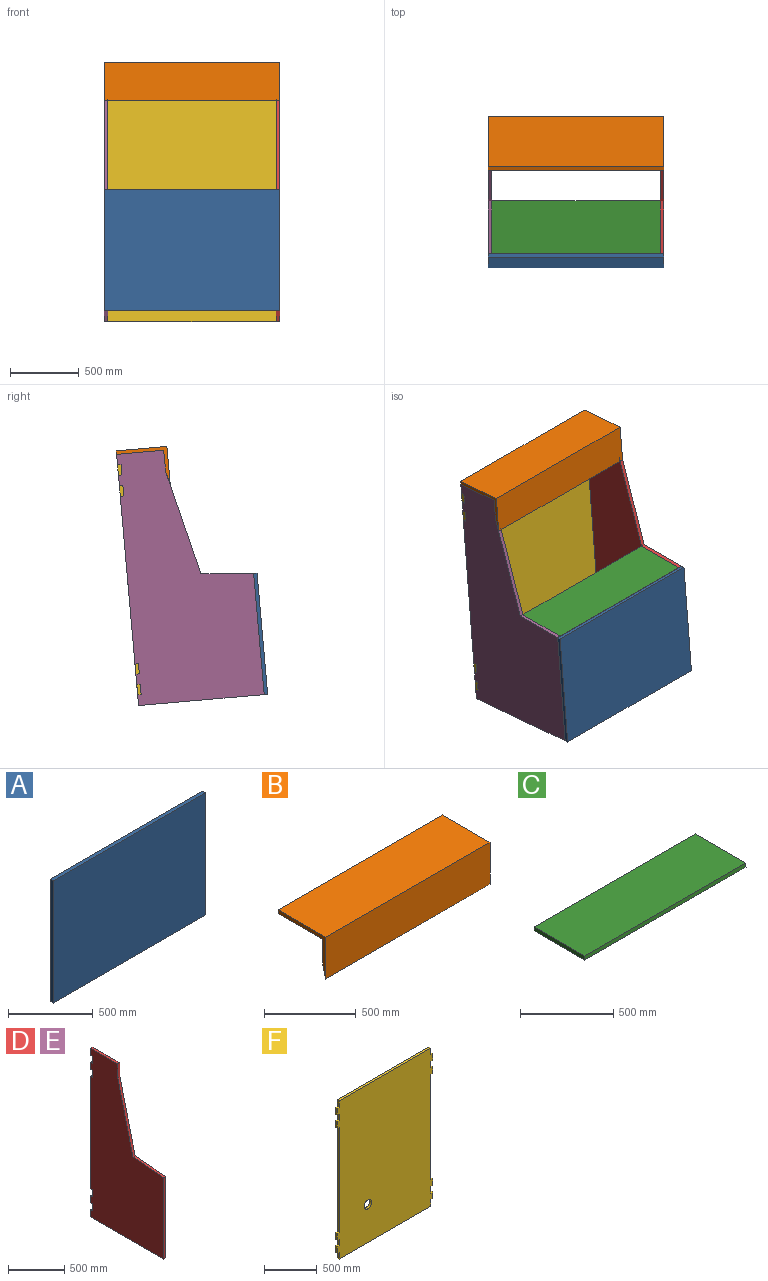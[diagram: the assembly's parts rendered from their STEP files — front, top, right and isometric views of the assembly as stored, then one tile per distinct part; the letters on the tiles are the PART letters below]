
ASSEMBLY  parts=6 mates=12
PART A: 6 faces, bbox 1270x25.4x881.1 mm
  f0: plane 881.07x25.4mm, normal (1,0,0), area 22379.1mm2, adj f1,f3,f4,f5
  f1: plane 1270x25.4mm, normal (0,0,1), area 32258mm2, adj f0,f2,f4,f5
  f2: plane 881.07x25.4mm, normal (-1,0,0), area 22379.1mm2, adj f1,f3,f4,f5
  f3: plane 1270x25.4mm, normal (0,0,-1), area 32258mm2, adj f0,f2,f4,f5
  f4: plane 1270x881.07mm, normal (0,-1,0), area 1118954.9mm2, adj f0,f1,f2,f3
  f5: plane 1270x881.07mm, normal (0,1,0), area 1118954.9mm2, adj f0,f1,f2,f3
PART B: 8 faces, bbox 1270x368.3x279.4 mm
  f0: plane 1270x342.9mm, normal (0,0,-1), area 435483mm2, adj f1,f2,f3,f6
  f1: plane 368.3x279.4mm, normal (1,0,0), area 14516.1mm2, adj f0,f2,f4,f5,f6,f7
  f2: plane 1270x25.4mm, normal (0,1,0), area 32258mm2, adj f0,f1,f3,f5
  f3: plane 368.3x279.4mm, normal (-1,0,0), area 14516.1mm2, adj f0,f2,f4,f5,f6,f7
  f4: plane 1270x279.4mm, normal (0,-1,0), area 354838mm2, adj f1,f3,f5,f7
  f5: plane 1270x368.3mm, normal (0,0,1), area 467741mm2, adj f1,f2,f3,f4
  f6: plane 1270x152.4mm, normal (0,1,0), area 193548mm2, adj f0,f1,f3,f7
  f7: plane 1270x101.6mm, normal (0,0.97,-0.24), area 133003.1mm2, adj f1,f3,f4,f6
PART C: 6 faces, bbox 1219.2x384.7x25.4 mm
  f0: plane 384.68x25.4mm, normal (1,0,0), area 9742.6mm2, adj f1,f3,f4,f5
  f1: plane 1219.2x25.4mm, normal (0,1,0), area 30967.7mm2, adj f0,f2,f3,f4
  f2: plane 384.68x25.4mm, normal (-1,0,0), area 9742.6mm2, adj f1,f3,f4,f5
  f3: plane 1219.2x382.46mm, normal (0,0,1), area 466289.6mm2, adj f0,f1,f2,f5
  f4: plane 1219.2x384.68mm, normal (0,0,-1), area 468998.9mm2, adj f0,f1,f2,f5
  f5: plane 1219.2x25.4mm, normal (0,-1,0.09), area 31086mm2, adj f0,f2,f3,f4
PART D: 25 faces, bbox 25.4x914.4x1828.8 mm
  f0: plane 76.2x25.4mm, normal (0,1,0), area 1935.5mm2, adj f4,f5,f20,f24
  f1: plane 1219.2x25.4mm, normal (0,1,0), area 30967.7mm2, adj f4,f5,f16,f19
  f2: plane 76.2x25.4mm, normal (0,1,0), area 1935.5mm2, adj f4,f5,f14,f18
  f3: plane 76.2x25.4mm, normal (0,1,0), area 1935.5mm2, adj f4,f5,f9,f13
  f4: plane 1828.8x914.4mm, normal (1,0,0), area 1208163.7mm2, adj f0,f1,f2,f3,f6,f7,f8,f9
  f5: plane 1828.8x914.4mm, normal (-1,0,0), area 1208163.7mm2, adj f0,f1,f2,f3,f6,f7,f8,f9
  f6: plane 762x190.5mm, normal (0,-0.97,0.24), area 19950.5mm2, adj f4,f5,f7,f12
  f7: plane 381x33.33mm, normal (0,-0.09,1), area 9714.4mm2, adj f4,f5,f6,f8
  f8: plane 881.07x25.4mm, normal (0,-1,0), area 22379.1mm2, adj f4,f5,f7,f9
  f9: plane 914.4x25.4mm, normal (0,0,-1), area 23225.8mm2, adj f3,f4,f5,f8
  f10: plane 76.2x25.4mm, normal (0,1,0), area 1935.5mm2, adj f4,f5,f11,f22
  f11: plane 342.9x25.4mm, normal (0,0,1), area 8709.7mm2, adj f4,f5,f10,f12
  f12: plane 152.4x25.4mm, normal (0,-1,0), area 3871mm2, adj f4,f5,f6,f11
  f13: plane 25.4x25.4mm, normal (0,0,1), area 645.2mm2, adj f3,f4,f5,f15
  f14: plane 25.4x25.4mm, normal (0,0,-1), area 645.2mm2, adj f2,f4,f5,f15
  f15: plane 76.2x25.4mm, normal (0,1,0), area 1935.5mm2, adj f4,f5,f13,f14
  f16: plane 25.4x25.4mm, normal (0,0,-1), area 645.2mm2, adj f1,f4,f5,f17
  f17: plane 76.2x25.4mm, normal (0,1,0), area 1935.5mm2, adj f4,f5,f16,f18
  f18: plane 25.4x25.4mm, normal (0,0,1), area 645.2mm2, adj f2,f4,f5,f17
  f19: plane 25.4x25.4mm, normal (0,0,1), area 645.2mm2, adj f1,f4,f5,f21
  f20: plane 25.4x25.4mm, normal (0,0,-1), area 645.2mm2, adj f0,f4,f5,f21
  f21: plane 76.2x25.4mm, normal (0,1,0), area 1935.5mm2, adj f4,f5,f19,f20
  f22: plane 25.4x25.4mm, normal (0,0,-1), area 645.2mm2, adj f4,f5,f10,f23
  f23: plane 76.2x25.4mm, normal (0,1,0), area 1935.5mm2, adj f4,f5,f22,f24
  f24: plane 25.4x25.4mm, normal (0,0,1), area 645.2mm2, adj f0,f4,f5,f23
PART E: same geometry as D
PART F: 39 faces, bbox 1270x25.4x1828.8 mm
  f0: plane 1219.2x25.4mm, normal (1,0,0), area 30967.7mm2, adj f12,f13,f30,f35
  f1: plane 76.2x25.4mm, normal (1,0,0), area 1935.5mm2, adj f12,f13,f33,f36
  f2: plane 76.2x25.4mm, normal (1,0,0), area 1935.5mm2, adj f12,f13,f26,f29
  f3: plane 76.2x25.4mm, normal (1,0,0), area 1935.5mm2, adj f9,f12,f13,f27
  f4: plane 76.2x25.4mm, normal (-1,0,0), area 1935.5mm2, adj f12,f13,f21,f24
  f5: plane 76.2x25.4mm, normal (-1,0,0), area 1935.5mm2, adj f11,f12,f13,f20
  f6: plane 1219.2x25.4mm, normal (-1,0,0), area 30967.7mm2, adj f12,f13,f18,f23
  f7: plane 76.2x25.4mm, normal (-1,0,0), area 1935.5mm2, adj f12,f13,f14,f17
  f8: plane 76.2x25.4mm, normal (1,0,0), area 1935.5mm2, adj f11,f12,f13,f32
  f9: plane 1219.2x25.4mm, normal (0,0,1), area 30967.7mm2, adj f3,f10,f12,f13
  f10: plane 76.2x25.4mm, normal (-1,0,0), area 1935.5mm2, adj f9,f12,f13,f15
  f11: plane 1219.2x25.4mm, normal (0,0,-1), area 30967.7mm2, adj f5,f8,f12,f13
  f12: plane 1828.8x1270mm, normal (0,-1,0), area 2237049.5mm2, adj f0,f1,f2,f3,f4,f5,f6,f7
  f13: plane 1828.8x1270mm, normal (0,1,0), area 2237049.5mm2, adj f0,f1,f2,f3,f4,f5,f6,f7
  f14: plane 25.4x25.4mm, normal (0,0,-1), area 645.2mm2, adj f7,f12,f13,f16
  f15: plane 25.4x25.4mm, normal (0,0,1), area 645.2mm2, adj f10,f12,f13,f16
  f16: plane 76.2x25.4mm, normal (-1,0,0), area 1935.5mm2, adj f12,f13,f14,f15
  f17: plane 25.4x25.4mm, normal (0,0,1), area 645.2mm2, adj f7,f12,f13,f19
  f18: plane 25.4x25.4mm, normal (0,0,-1), area 645.2mm2, adj f6,f12,f13,f19
  f19: plane 76.2x25.4mm, normal (-1,0,0), area 1935.5mm2, adj f12,f13,f17,f18
  f20: plane 25.4x25.4mm, normal (0,0,-1), area 645.2mm2, adj f5,f12,f13,f22
  f21: plane 25.4x25.4mm, normal (0,0,1), area 645.2mm2, adj f4,f12,f13,f22
  f22: plane 76.2x25.4mm, normal (-1,0,0), area 1935.5mm2, adj f12,f13,f20,f21
  f23: plane 25.4x25.4mm, normal (0,0,1), area 645.2mm2, adj f6,f12,f13,f25
  f24: plane 25.4x25.4mm, normal (0,0,-1), area 645.2mm2, adj f4,f12,f13,f25
  f25: plane 76.2x25.4mm, normal (-1,0,0), area 1935.5mm2, adj f12,f13,f23,f24
  f26: plane 25.4x25.4mm, normal (0,0,-1), area 645.2mm2, adj f2,f12,f13,f28
  f27: plane 25.4x25.4mm, normal (0,0,1), area 645.2mm2, adj f3,f12,f13,f28
  f28: plane 76.2x25.4mm, normal (1,0,0), area 1935.5mm2, adj f12,f13,f26,f27
  f29: plane 25.4x25.4mm, normal (0,0,1), area 645.2mm2, adj f2,f12,f13,f31
  f30: plane 25.4x25.4mm, normal (0,0,-1), area 645.2mm2, adj f0,f12,f13,f31
  f31: plane 76.2x25.4mm, normal (1,0,0), area 1935.5mm2, adj f12,f13,f29,f30
  f32: plane 25.4x25.4mm, normal (0,0,-1), area 645.2mm2, adj f8,f12,f13,f34
  f33: plane 25.4x25.4mm, normal (0,0,1), area 645.2mm2, adj f1,f12,f13,f34
  f34: plane 76.2x25.4mm, normal (1,0,0), area 1935.5mm2, adj f12,f13,f32,f33
  f35: plane 25.4x25.4mm, normal (0,0,1), area 645.2mm2, adj f0,f12,f13,f37
  f36: plane 25.4x25.4mm, normal (0,0,-1), area 645.2mm2, adj f1,f12,f13,f37
  f37: plane 76.2x25.4mm, normal (1,0,0), area 1935.5mm2, adj f12,f13,f35,f36
  f38: cylinder r=50.8mm len=101.6mm, axis (0,-1,0), area 8107.3mm2, adj f12,f13
PLACE A rot(axis=(-1,0,0),5deg) t=(-345.24,-558.31,79.39)mm
PLACE B rot(axis=(-1,0,0),5deg) t=(-345.24,290.16,1398.72)mm
PLACE C t=(-345.24,-328.69,492.84)mm
PLACE D rot(axis=(-1,0,0),5deg) t=(264.36,-101.4,56.14)mm
PLACE E rot(axis=(-1,0,0),5deg) t=(-980.24,-101.4,56.14)mm
PLACE F rot(axis=(-1,0,0),5deg) t=(-345.24,393.91,471.75)mm
MATE planar B.f0 <-> F.f9  axis (0,-0.09,-1) through (-345.24,302.81,1397.62)mm
MATE planar E.f8 <-> A.f5  axis (0,-1,0.09) through (-967.54,-558.31,79.39)mm
MATE fastened F.f35 <-> D.f16  axis (0,0.09,1) through (277.06,328.13,-134.42)mm
MATE fastened F.f23 <-> E.f16  axis (0,0.09,1) through (-967.54,328.13,-134.42)mm
MATE planar C.f2 <-> E.f4  axis (-1,0,0) through (-954.84,-329.24,505.53)mm
MATE parallel C.f3 <-> E.f7  axis (0,0,1) through (-345.24,-328.69,518.24)mm
MATE planar C.f5 <-> A.f5  axis (0,-1,0.09) through (-345.24,-521.03,505.54)mm
MATE planar A.f3 <-> F.f11  axis (0,-0.09,-1) through (-345.24,-609.36,-358.36)mm
MATE planar E.f7 <-> C.f3  axis (0,0,1) through (-967.54,-328.69,518.24)mm
MATE fastened E.f5 <-> B.f3  axis (-1,0,0) through (-980.24,125.37,1336.65)mm
MATE planar A.f0 <-> D.f4  axis (1,0,0) through (289.76,-570.96,80.49)mm
MATE planar E.f4 <-> C.f2  axis (1,0,0) through (-954.84,-1.64,323.22)mm
